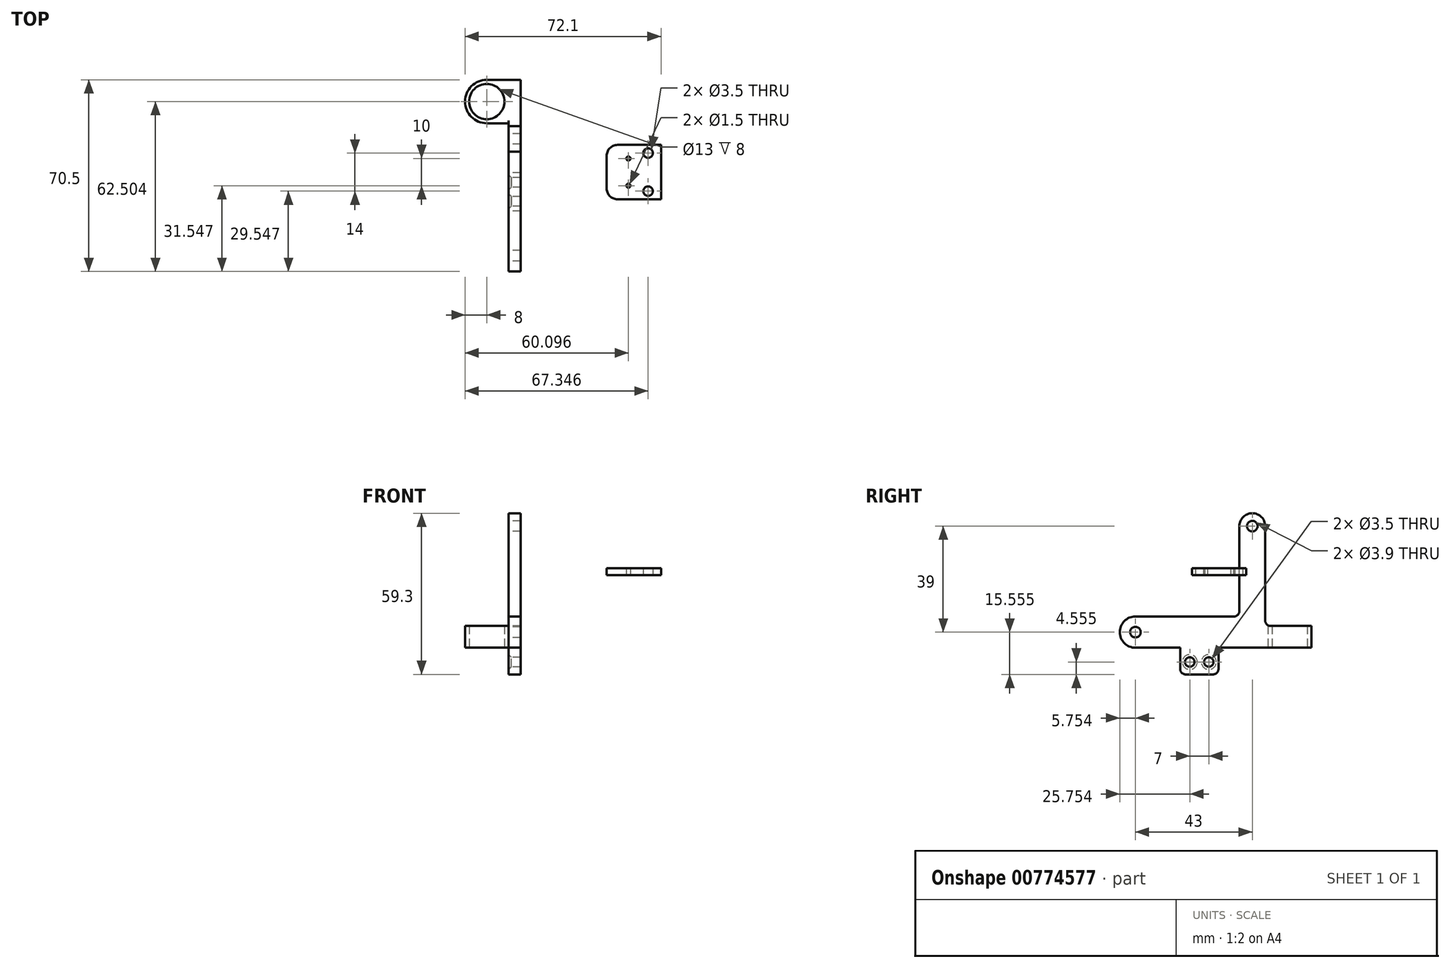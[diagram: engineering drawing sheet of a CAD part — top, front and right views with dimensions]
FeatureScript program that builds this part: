
annotation { "Feature Type Name" : "Feature", "Feature Type Description" : "" }
export const myFeature = defineFeature(function(context is Context, id is Id, definition is map)
    precondition{}
    {
        {
            var Q0;
            Q0=qCreatedBy(makeId("Right.planeOp"),FACE);
            var sketch = newSketch(context, id + "F0", { "sketchPlane" : qUnion([Q0])});
            skLineSegment(sketch, "E0.top", {"start": v(15.62, -36.73) * mm, "end": v(1.12, -36.73) * mm, "construction": true});
            skLineSegment(sketch, "E0.left", {"start": v(15.62, -26.73) * mm, "end": v(15.62, -36.73) * mm, "construction": true});
            skLineSegment(sketch, "E0.right", {"start": v(1.12, -26.73) * mm, "end": v(1.12, -36.73) * mm, "construction": true});
            skLineSegment(sketch, "E1", {"start": v(1.12, -26.73) * mm, "end": v(-21.88, -26.73) * mm, "construction": true});
            skLineSegment(sketch, "E2", {"start": v(-21.88, -26.73) * mm, "end": v(-21.88, 22.77) * mm, "construction": true});
            skLineSegment(sketch, "E3", {"start": v(-21.88, 22.77) * mm, "end": v(36.62, 22.77) * mm, "construction": true});
            skLineSegment(sketch, "E4", {"start": v(36.62, 22.77) * mm, "end": v(36.62, -26.73) * mm, "construction": true});
            skLineSegment(sketch, "E5", {"start": v(36.62, -26.73) * mm, "end": v(15.62, -26.73) * mm, "construction": true});
            skCircle(sketch, "E6", {"center": v(-15.13, -20.98) * mm, "radius": 1.75 * mm, "construction": true});
            skCircle(sketch, "E7", {"center": v(27.87, 18.02) * mm, "radius": 1.75 * mm, "construction": true});
            skPoint(sketch, "E8", {"position": v(27.87, 19.77) * mm});
            skPoint(sketch, "E9", {"position": v(29.62, 18.02) * mm});
            skPoint(sketch, "E10", {"position": v(-16.88, -20.98) * mm});
            skPoint(sketch, "E11", {"position": v(-15.13, -22.73) * mm});
            skCircle(sketch, "E12", {"center": v(4.87, -31.98) * mm, "radius": 1.75 * mm, "construction": true});
            skCircle(sketch, "E13", {"center": v(11.87, -31.98) * mm, "radius": 1.75 * mm, "construction": true});
            skPoint(sketch, "E14", {"position": v(3.12, -31.98) * mm});
            skPoint(sketch, "E15", {"position": v(13.62, -31.98) * mm});
            skPoint(sketch, "E16", {"position": v(11.87, -33.73) * mm});
            skPoint(sketch, "E17", {"position": v(4.87, -33.73) * mm});
            skPoint(sketch, "E18", {"position": v(10.12, -31.98) * mm});
            skPoint(sketch, "E19", {"position": v(6.62, -31.98) * mm});
            skSolve(sketch);
        }
        {
            var Q0;
            Q0=sQuery(id+"F0.wireOp",EDGE,"E5");
            cPlane(context, id + "F1", {"entities" : qUnion([Q0]), "cplaneType" : CPlaneType.LINE_ANGLE, "offset" : 25 * mm, "angle" : 0 * degree, "width" : 150 * mm, "height" : 150 * mm});
        }
        {
            var Q0;
            Q0=qCreatedBy(id+"F1.planeOp",FACE);
            var sketch = newSketch(context, id + "F2", { "sketchPlane" : qUnion([Q0])});
            skCircle(sketch, "E20", {"center": v(-8, -41.62) * mm, "radius": 6 * mm, "construction": true});
            skCircle(sketch, "E21", {"center": v(-8, -41.62) * mm, "radius": 6.5 * mm});
            skLineSegment(sketch, "E22", {"start": v(-8, -62.6) * mm, "end": v(-8, -28.81) * mm, "construction": true});
            skLineSegment(sketch, "E23", {"start": v(-8, -49.62) * mm, "end": v(0, -49.62) * mm});
            skLineSegment(sketch, "E24", {"start": v(0, -49.62) * mm, "end": v(0, -33.62) * mm});
            skLineSegment(sketch, "E25", {"start": v(0, -33.62) * mm, "end": v(-8, -33.62) * mm});
            skLineSegment(sketch, "E26", {"start": v(-89.02, -41.62) * mm, "end": v(-73.96, -41.62) * mm, "construction": true});
            skArc(sketch, "E27", {"start": v(-8, -49.62) * mm, "mid": v(-16, -41.62) * mm, "end": v(-8, -33.62) * mm});
            skArc(sketch, "E28", {"start": v(-8, -33.62) * mm, "mid": v(0, -41.62) * mm, "end": v(-8, -49.62) * mm});
            skPoint(sketch, "E29", {"position": v(0, -41.62) * mm});
            skSolve(sketch);
        }
        {
            var Q0;
            Q0=qCreatedBy(makeId("Right.planeOp"),FACE);
            var sketch = newSketch(context, id + "F3", { "sketchPlane" : qUnion([Q0])});
            skLineSegment(sketch, "E30.bottom", {"start": v(49.62, -18.73) * mm, "end": v(36.62, -18.73) * mm});
            skLineSegment(sketch, "E30.top", {"start": v(49.62, -26.73) * mm, "end": v(36.62, -26.73) * mm});
            skLineSegment(sketch, "E30.left", {"start": v(49.62, -18.73) * mm, "end": v(49.62, -26.73) * mm});
            skLineSegment(sketch, "E30.right", {"start": v(36.62, -18.73) * mm, "end": v(36.62, -26.73) * mm});
            skLineSegment(sketch, "E31", {"start": v(36.62, -26.73) * mm, "end": v(15.42, -26.73) * mm});
            skLineSegment(sketch, "E32", {"start": v(15.42, -26.73) * mm, "end": v(15.42, -36.53) * mm});
            skLineSegment(sketch, "E33", {"start": v(15.42, -36.53) * mm, "end": v(1.32, -36.53) * mm});
            skLineSegment(sketch, "E34", {"start": v(1.32, -36.53) * mm, "end": v(1.32, -26.73) * mm});
            skLineSegment(sketch, "E35", {"start": v(1.32, -26.73) * mm, "end": v(-15.13, -26.73) * mm});
            skCircle(sketch, "E36", {"center": v(-15.13, -20.98) * mm, "radius": 1.95 * mm});
            skArc(sketch, "E37", {"start": v(-15.13, -26.73) * mm, "mid": v(-20.88, -20.98) * mm, "end": v(-15.13, -15.23) * mm});
            skCircle(sketch, "E38", {"center": v(27.87, 18.02) * mm, "radius": 1.95 * mm});
            skCircle(sketch, "E39", {"center": v(4.87, -31.98) * mm, "radius": 1.75 * mm});
            skCircle(sketch, "E40", {"center": v(11.87, -31.98) * mm, "radius": 1.75 * mm});
            skLineSegment(sketch, "E41", {"start": v(-15.13, -15.23) * mm, "end": v(21.12, -15.23) * mm});
            skLineSegment(sketch, "E42", {"start": v(23.12, -13.23) * mm, "end": v(23.12, 18.02) * mm});
            skArc(sketch, "E43", {"start": v(23.12, 18.02) * mm, "mid": v(27.87, 22.77) * mm, "end": v(32.62, 18.02) * mm});
            skLineSegment(sketch, "E44", {"start": v(32.62, 18.02) * mm, "end": v(32.62, -16.73) * mm});
            skLineSegment(sketch, "E45", {"start": v(34.62, -18.73) * mm, "end": v(36.62, -18.73) * mm});
            skPoint(sketch, "E46.visualSharp", {"position": v(32.62, -18.73) * mm});
            skArc(sketch, "E46.filletArc", {"start": v(32.62, -16.73) * mm, "mid": v(33.2, -18.14) * mm, "end": v(34.62, -18.73) * mm});
            skPoint(sketch, "E47.visualSharp", {"position": v(23.12, -15.23) * mm});
            skArc(sketch, "E47.filletArc", {"start": v(21.12, -15.23) * mm, "mid": v(22.54, -14.64) * mm, "end": v(23.12, -13.23) * mm});
            skSolve(sketch);
        }
        {
            var Q0;
            Q0=makeQuery(id+"F3.imprint","IMPRINT",FACE,{"disambiguationData":[TD([[makeQuery(id+"F3.imprint","IMPRINT",EDGE,{"derivedFrom":sQuery(id+"F3.wireOp",EDGE,"E30.right")}),-1.0]])]});
            var Q1;
            Q1=makeQuery(id+"F3.imprint","IMPRINT",FACE,{"disambiguationData":[TD([[makeQuery(id+"F3.imprint","IMPRINT",EDGE,{"derivedFrom":sQuery(id+"F3.wireOp",EDGE,"E30.bottom")}),1.0]])]});
            extrude(context, id + "F4", {"entities" : qUnion([Q0, Q1]), "depth" : 4.5 * mm, "offsetDistance" : 25 * mm});
        }
        {
            var Q0;
            Q0=makeQuery(id+"F2.imprint","IMPRINT",FACE,{"disambiguationData":[TD([[makeQuery(id+"F2.imprint","IMPRINT",EDGE,{"derivedFrom":sQuery(id+"F2.wireOp",EDGE,"E21")}),-1.0]])]});
            var Q1;
            {var subQ0=sQuery(id+"F2.wireOp",EDGE,"E23");Q1=makeQuery(id+"F2.imprint","IMPRINT",FACE,{"disambiguationData":[TD([[makeQuery(id+"F2.imprint","IMPRINT",EDGE,{"derivedFrom":subQ0}),1.0]])]});}
            var Q2;
            {var subQ0=sQuery(id+"F2.wireOp",EDGE,"E25");Q2=makeQuery(id+"F2.imprint","IMPRINT",FACE,{"disambiguationData":[TD([[makeQuery(id+"F2.imprint","IMPRINT",EDGE,{"derivedFrom":subQ0}),1.0]])]});}
            var Q3;
            Q3=makeQuery(id+"F4.opExtrude","CAP_VERTEX",VERTEX,{"disambiguationData":[OSD([sQuery(id+"F3.wireOp",EDGE,"E30.bottom"),sQuery(id+"F3.wireOp",EDGE,"E30.left")])],"isStart":true});
            extrude(context, id + "F5", {"entities" : qUnion([Q0, Q1, Q2]), "operationType" : NewBodyOperationType.ADD, "endBound" : BoundingType.UP_TO_VERTEX, "oppositeDirection" : true, "depth" : 25 * mm, "endBoundEntityVertex" : qUnion([Q3]), "offsetDistance" : 25 * mm});
        }
        {
            var Q0;
            Q0=makeQuery(id+"F4.opExtrude","CAP_EDGE",EDGE,{"disambiguationData":[OSD([sQuery(id+"F3.wireOp",EDGE,"E39")])],"isStart":true});
            var Q1;
            Q1=makeQuery(id+"F4.opExtrude","CAP_EDGE",EDGE,{"disambiguationData":[OSD([sQuery(id+"F3.wireOp",EDGE,"E40")])],"isStart":true});
            chamfer(context, id + "F6", {"entities" : qUnion([Q0, Q1]), "width" : 1 * mm, "tangentPropagation" : true});
        }
        {
            var Q0;
            Q0=makeQuery(id+"F4.opExtrude","SWEPT_EDGE",EDGE,{"disambiguationData":[OSD([sQuery(id+"F3.wireOp",EDGE,"E32"),sQuery(id+"F3.wireOp",EDGE,"E33")])]});
            var Q1;
            Q1=makeQuery(id+"F4.opExtrude","SWEPT_EDGE",EDGE,{"disambiguationData":[OSD([sQuery(id+"F3.wireOp",EDGE,"E33"),sQuery(id+"F3.wireOp",EDGE,"E34")])]});
            fillet(context, id + "F7", {"entities" : qUnion([Q0, Q1]), "radius" : 2 * mm, "tangentPropagation" : true, "allowEdgeOverflow" : false});
        }
        {
            var Q0;
            Q0=qCreatedBy(makeId("Top.planeOp"),FACE);
            var sketch = newSketch(context, id + "F8", { "sketchPlane" : qUnion([Q0])});
            skCircle(sketch, "E48", {"center": v(51.35, 22.67) * mm, "radius": 1.75 * mm});
            skCircle(sketch, "E49", {"center": v(51.35, 8.67) * mm, "radius": 1.75 * mm});
            skLineSegment(sketch, "E50.bottom", {"start": v(56.1, 25.67) * mm, "end": v(40.1, 25.67) * mm});
            skLineSegment(sketch, "E50.top", {"start": v(56.1, 5.67) * mm, "end": v(40.1, 5.67) * mm});
            skLineSegment(sketch, "E50.left", {"start": v(56.1, 25.67) * mm, "end": v(56.1, 5.67) * mm});
            skLineSegment(sketch, "E50.right", {"start": v(36.1, 21.67) * mm, "end": v(36.1, 9.67) * mm});
            skLineSegment(sketch, "E51", {"start": v(29.06, 15.67) * mm, "end": v(65.68, 15.67) * mm, "construction": true});
            skCircle(sketch, "E52", {"center": v(44.1, 10.67) * mm, "radius": 0.75 * mm});
            skCircle(sketch, "E53", {"center": v(44.1, 20.67) * mm, "radius": 0.75 * mm});
            skPoint(sketch, "E54.visualSharp", {"position": v(36.1, 25.67) * mm});
            skArc(sketch, "E54.filletArc", {"start": v(40.1, 25.67) * mm, "mid": v(37.27, 24.5) * mm, "end": v(36.1, 21.67) * mm});
            skPoint(sketch, "E55.visualSharp", {"position": v(36.1, 5.67) * mm});
            skArc(sketch, "E55.filletArc", {"start": v(36.1, 9.67) * mm, "mid": v(37.27, 6.84) * mm, "end": v(40.1, 5.67) * mm});
            skLineSegment(sketch, "E56", {"start": v(46.1, 32.42) * mm, "end": v(46.1, 3.7) * mm, "construction": true});
            skSolve(sketch);
        }
        {
            var Q0;
            Q0=makeQuery(id+"F8.imprint","IMPRINT",FACE,{"disambiguationData":[TD([[makeQuery(id+"F8.imprint","IMPRINT",EDGE,{"derivedFrom":sQuery(id+"F8.wireOp",EDGE,"E48")}),-1.0]])]});
            extrude(context, id + "F9", {"entities" : qUnion([Q0]), "depth" : 2.5 * mm, "offsetDistance" : 25 * mm});
        }
    });
